# Revit family: Wall-Screen-Fixed-Vertical_Blade-LS-52V-CSR-3
name_source: partatom
category: Specialty Equipment
units: mm (PartAtom-declared; Revit-internal decimal feet)

## family parameters
Cut with Voids When Loaded = No
Host = Face
OmniClass Number = 23.40.10.24.14
OmniClass Title = Screens and Louvers
Part Type = Normal
Room Calculation Point = No
Round Connector Dimension = Use Diameter
Shared = No

## types (1)
- LS-52V Wall Screen
    Assembly Code = B2010300
    CD_Blade Spacing = 0' - 2"
    CD_Center Support = Yes
    CD_Depth = 0' - 7"
    CD_Finish = Metal-Aluminum-AWV-Kynar-Standard-Sante_Fe_Red
    CD_Height = 5' - 0"
    CD_Height Max = 8' - 0"
    CD_Height Min = 1' - 0"
    CD_Louver Array Control = 26
    CD_Product Documentation Link = https://awv-cdn.nyc3.digitaloceanspaces.com
    CD_Product Name = Sightproof Equipment Screen
    CD_Product Page URL = https://awv.com
    CD_Requested Height = 5' - 0"
    CD_Requested Width = 5' - 0"
    CD_Warranty = https://awv-cdn.nyc3.digitaloceanspaces.com
    CD_Width = 5' - 0"
    CD_Width Max = 8' - 0"
    CD_Width Min = 1' - 0"
    Default Elevation = 8' - 0"
    Description = 6063-T5 Extruded Aluminum Frame and Blades
    Manufacturer = American Warming and Ventilation
    Model = LS-52V
    Type Comments = Vertical Sight Proof Blade
    URL = https://awv.com

## geometry (parser evidence)
native form markers: Sweep x5
no freeform markers — native parametric forms only
